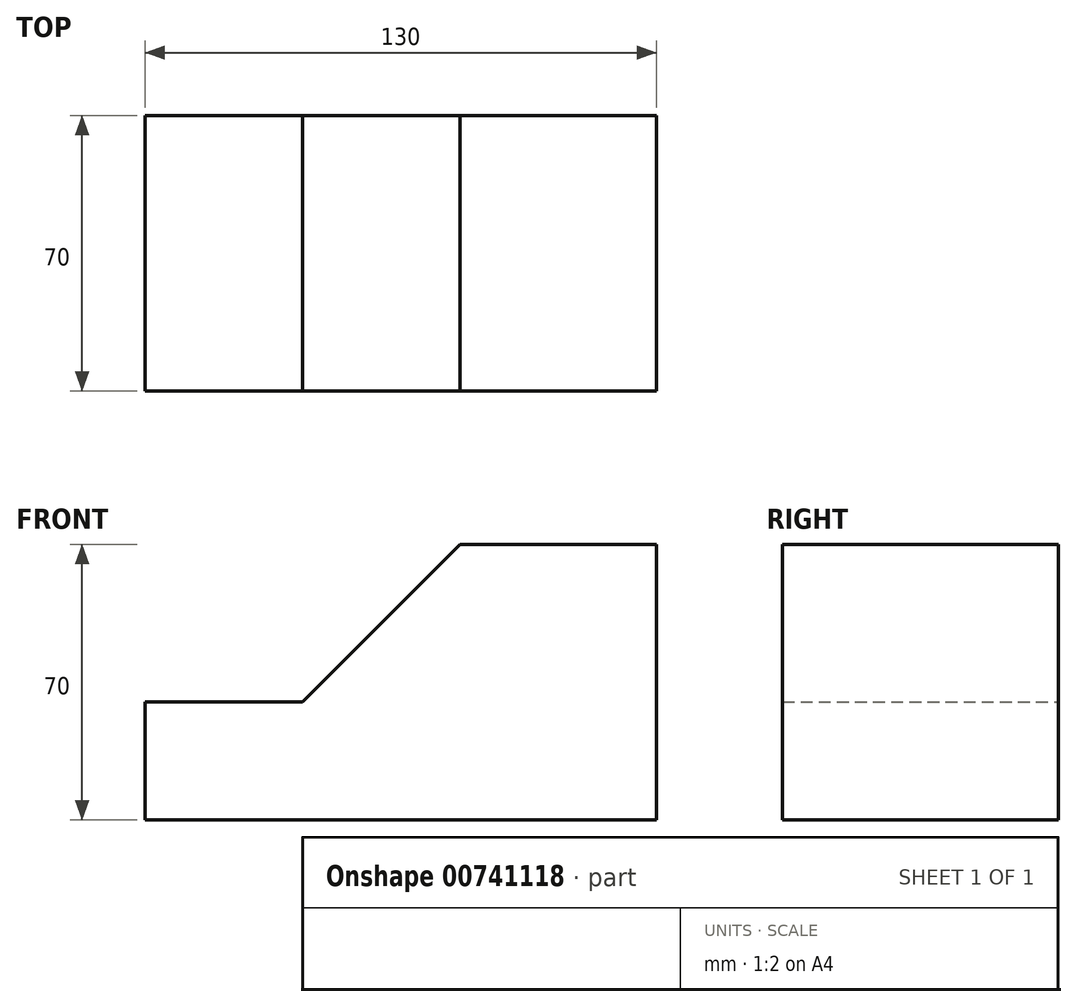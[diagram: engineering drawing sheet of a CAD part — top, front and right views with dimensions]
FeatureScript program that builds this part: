
annotation { "Feature Type Name" : "Feature", "Feature Type Description" : "" }
export const myFeature = defineFeature(function(context is Context, id is Id, definition is map)
    precondition{}
    {
        {
            var Q0;
            Q0=qCreatedBy(makeId("Front.planeOp"),FACE);
            var sketch = newSketch(context, id + "F0", { "sketchPlane" : qUnion([Q0])});
            skLineSegment(sketch, "E0.bottom", {"start": v(15, 35) * mm, "end": v(65, 35) * mm});
            skLineSegment(sketch, "E0.top", {"start": v(-65, -35) * mm, "end": v(65, -35) * mm});
            skLineSegment(sketch, "E0.right", {"start": v(65, 35) * mm, "end": v(65, -35) * mm});
            skPoint(sketch, "E0.middle", {"position": v(0, 0) * mm});
            skLineSegment(sketch, "E1", {"start": v(65, 35) * mm, "end": v(15, 35) * mm});
            skLineSegment(sketch, "E2", {"start": v(-65, -35) * mm, "end": v(-65, -5) * mm});
            skLineSegment(sketch, "E3", {"start": v(-65, -5) * mm, "end": v(-25, -5) * mm});
            skLineSegment(sketch, "E4", {"start": v(-25, -5) * mm, "end": v(15, 35) * mm});
            skPoint(sketch, "E5.orphan", {"position": v(-65, 35) * mm});
            skSolve(sketch);
        }
        {
            var Q0;
            Q0=makeQuery(id+"F0.imprint","IMPRINT",FACE,{"disambiguationData":[TD([[makeQuery(id+"F0.imprint","IMPRINT",EDGE,{"derivedFrom":sQuery(id+"F0.wireOp",EDGE,"E0.top")}),1.0]])]});
            extrude(context, id + "F1", {"entities" : qUnion([Q0]), "endBound" : BoundingType.SYMMETRIC, "depth" : 70 * mm, "offsetDistance" : 25 * mm});
        }
    });
